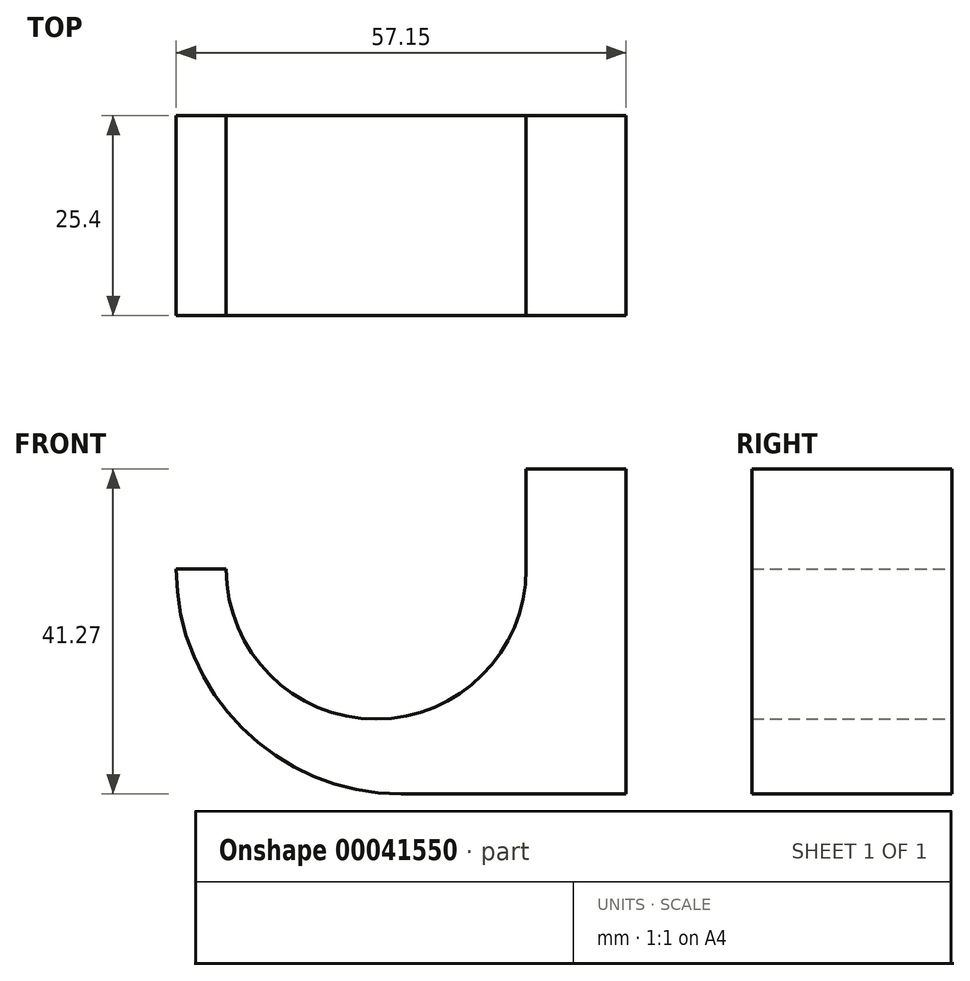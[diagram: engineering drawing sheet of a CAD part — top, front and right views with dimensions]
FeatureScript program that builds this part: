
annotation { "Feature Type Name" : "Feature", "Feature Type Description" : "" }
export const myFeature = defineFeature(function(context is Context, id is Id, definition is map)
    precondition{}
    {
        {
            var Q0;
            Q0=qCreatedBy(makeId("Front.planeOp"),FACE);
            var sketch = newSketch(context, id + "F0", { "sketchPlane" : qUnion([Q0])});
            skLineSegment(sketch, "E0", {"start": v(57.15, 0) * mm, "end": v(57.15, 12.7) * mm});
            skLineSegment(sketch, "E1", {"start": v(57.15, 12.7) * mm, "end": v(44.45, 12.7) * mm});
            skLineSegment(sketch, "E2", {"start": v(44.45, 12.7) * mm, "end": v(44.45, 0) * mm});
            skArc(sketch, "E3", {"start": v(6.35, 0) * mm, "mid": v(25.4, -19.05) * mm, "end": v(44.45, 0) * mm});
            skLineSegment(sketch, "E4", {"start": v(0, 0) * mm, "end": v(6.35, 0) * mm});
            skArc(sketch, "E5", {"start": v(0, 0) * mm, "mid": v(28.58, -28.58) * mm, "end": v(57.15, 0) * mm});
            skPoint(sketch, "E5.endSnap0", {"position": v(3.17, 0) * mm});
            skLineSegment(sketch, "E6", {"start": v(28.58, -28.58) * mm, "end": v(57.15, -28.58) * mm});
            skLineSegment(sketch, "E7", {"start": v(57.15, -28.58) * mm, "end": v(57.15, 0) * mm});
            skSolve(sketch);
        }
        {
            var Q0;
            Q0 = qSketchRegion(id + "F0", true);
            extrude(context, id + "F1", {"entities" : qUnion([Q0]), "depth" : 25.4 * mm});
        }
    });
